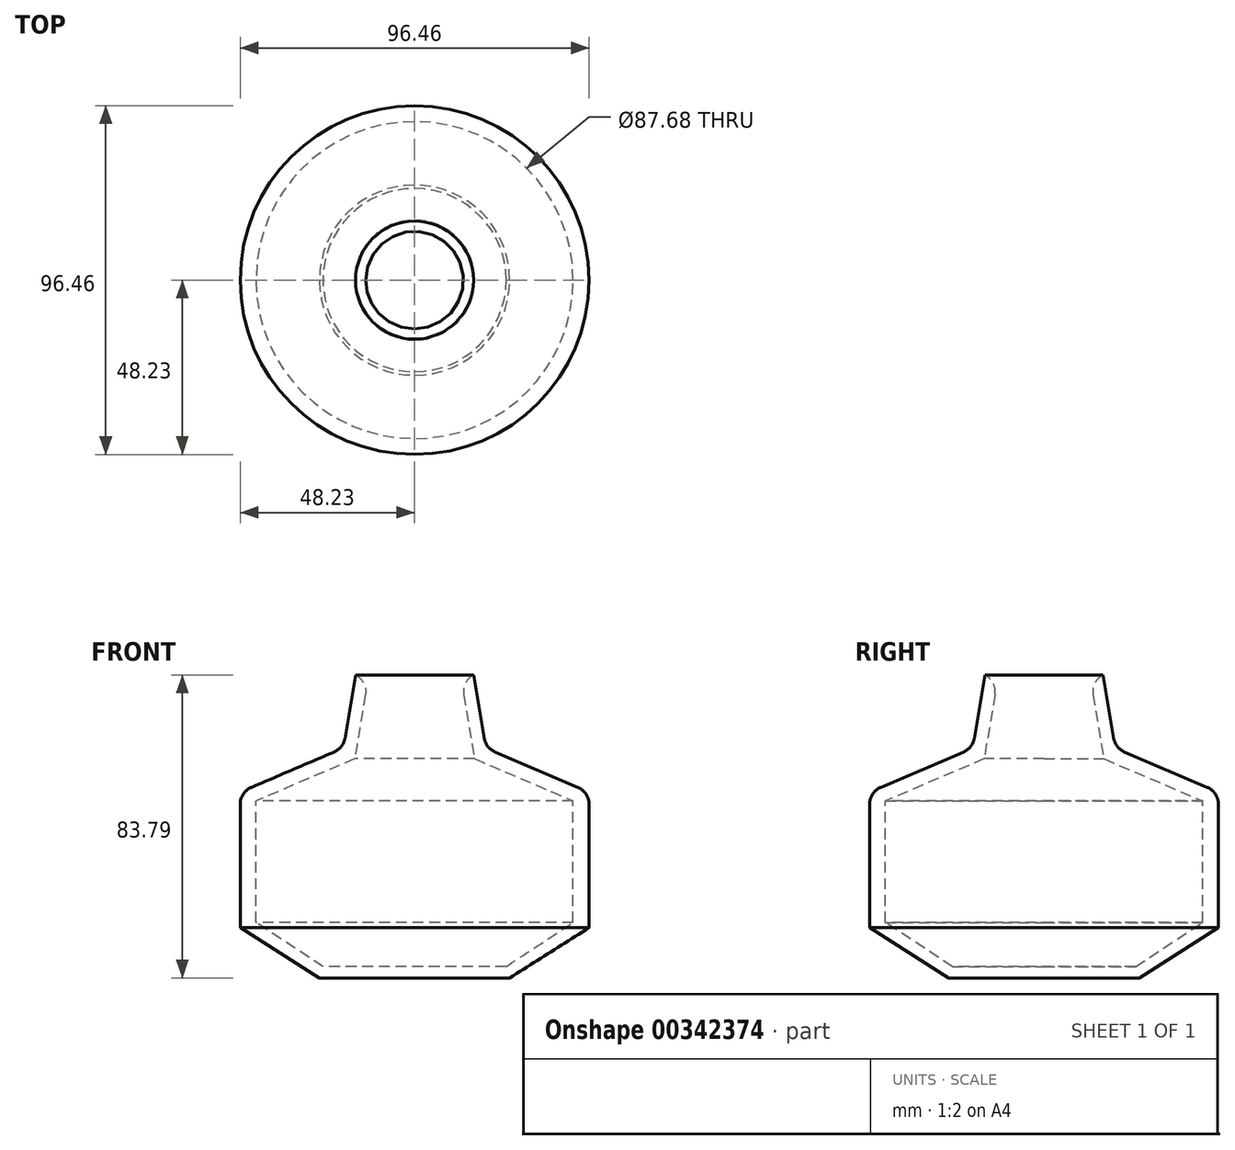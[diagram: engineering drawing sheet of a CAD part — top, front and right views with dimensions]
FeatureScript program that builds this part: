
annotation { "Feature Type Name" : "Feature", "Feature Type Description" : "" }
export const myFeature = defineFeature(function(context is Context, id is Id, definition is map)
    precondition{}
    {
        {
            var Q0;
            Q0=qCreatedBy(makeId("Front.planeOp"),FACE);
            var sketch = newSketch(context, id + "F0", { "sketchPlane" : qUnion([Q0])});
            skLineSegment(sketch, "E0", {"start": v(-16.32, 37.39) * mm, "end": v(-19.73, 17.17) * mm});
            skLineSegment(sketch, "E1", {"start": v(-19.73, 17.17) * mm, "end": v(-48.23, 5) * mm});
            skLineSegment(sketch, "E2", {"start": v(-48.23, 5) * mm, "end": v(-48.23, -32.52) * mm});
            skLineSegment(sketch, "E3", {"start": v(-48.23, -32.52) * mm, "end": v(-26.3, -46.4) * mm});
            skLineSegment(sketch, "E4", {"start": v(-26.3, -46.4) * mm, "end": v(0, -46.4) * mm});
            skLineSegment(sketch, "E5", {"start": v(0, -46.4) * mm, "end": v(0, -43.23) * mm});
            skLineSegment(sketch, "E6", {"start": v(0, -43.23) * mm, "end": v(-25.33, -43.23) * mm});
            skLineSegment(sketch, "E7", {"start": v(-25.33, -43.23) * mm, "end": v(-43.84, -31.05) * mm});
            skLineSegment(sketch, "E8", {"start": v(-43.84, -31.05) * mm, "end": v(-43.84, 2.56) * mm});
            skLineSegment(sketch, "E9", {"start": v(-43.84, 2.56) * mm, "end": v(-16.58, 14.2) * mm});
            skLineSegment(sketch, "E10", {"start": v(-16.58, 14.2) * mm, "end": v(-12.71, 37.15) * mm});
            skLineSegment(sketch, "E11", {"start": v(-12.71, 37.15) * mm, "end": v(-16.32, 37.39) * mm});
            skSolve(sketch);
        }
        {
            var Q0;
            Q0=qCreatedBy(makeId("Front.planeOp"),FACE);
            var sketch = newSketch(context, id + "F1", { "sketchPlane" : qUnion([Q0])});
            skLineSegment(sketch, "E12", {"start": v(0, 42.5) * mm, "end": v(0, -50.78) * mm, "construction": true});
            skSolve(sketch);
        }
        {
            var Q0;
            Q0=makeQuery(id+"F0.imprint","IMPRINT",FACE,{"disambiguationData":[TD([[makeQuery(id+"F0.imprint","IMPRINT",EDGE,{"derivedFrom":sQuery(id+"F0.wireOp",EDGE,"E0")}),1.0]])]});
            var Q1;
            Q1=sQuery(id+"F1.wireOp",EDGE,"E12");
            revolve(context, id + "F2", {"entities" : qUnion([Q0]), "axis" : qUnion([Q1]), "revolveType" : RevolveType.FULL});
        }
        {
            var Q0;
            Q0=makeQuery(id+"F2.opRevolve","SWEPT_EDGE",EDGE,{"disambiguationData":[OSD([sQuery(id+"F0.wireOp",EDGE,"E0"),sQuery(id+"F0.wireOp",EDGE,"E1")])]});
            var Q1;
            Q1=makeQuery(id+"F2.opRevolve","SWEPT_EDGE",EDGE,{"disambiguationData":[OSD([sQuery(id+"F0.wireOp",EDGE,"E1"),sQuery(id+"F0.wireOp",EDGE,"E2")])]});
            fillet(context, id + "F3", {"entities" : qUnion([Q0, Q1]), "radius" : 5.08 * mm, "tangentPropagation" : true, "allowEdgeOverflow" : false});
        }
        {
            var Q0;
            Q0=makeQuery(id+"F2.opRevolve","SWEPT_EDGE",EDGE,{"disambiguationData":[OSD([sQuery(id+"F0.wireOp",EDGE,"E10"),sQuery(id+"F0.wireOp",EDGE,"E11")])]});
            fillet(context, id + "F4", {"entities" : qUnion([Q0]), "radius" : 5.08 * mm, "tangentPropagation" : true, "allowEdgeOverflow" : false});
        }
        {
            var Q0;
            Q0=qCreatedBy(makeId("Right.planeOp"),FACE);
            cPlane(context, id + "F5", {"entities" : qUnion([Q0]), "cplaneType" : CPlaneType.OFFSET, "offset" : 48.26 * mm, "width" : 152.4 * mm, "height" : 152.4 * mm});
        }
        {
            var Q0;
            Q0=qCreatedBy(makeId("Top.planeOp"),FACE);
            cPlane(context, id + "F6", {"entities" : qUnion([Q0]), "cplaneType" : CPlaneType.OFFSET, "offset" : 34.54 * mm, "width" : 152.4 * mm, "height" : 152.4 * mm});
        }
    });
